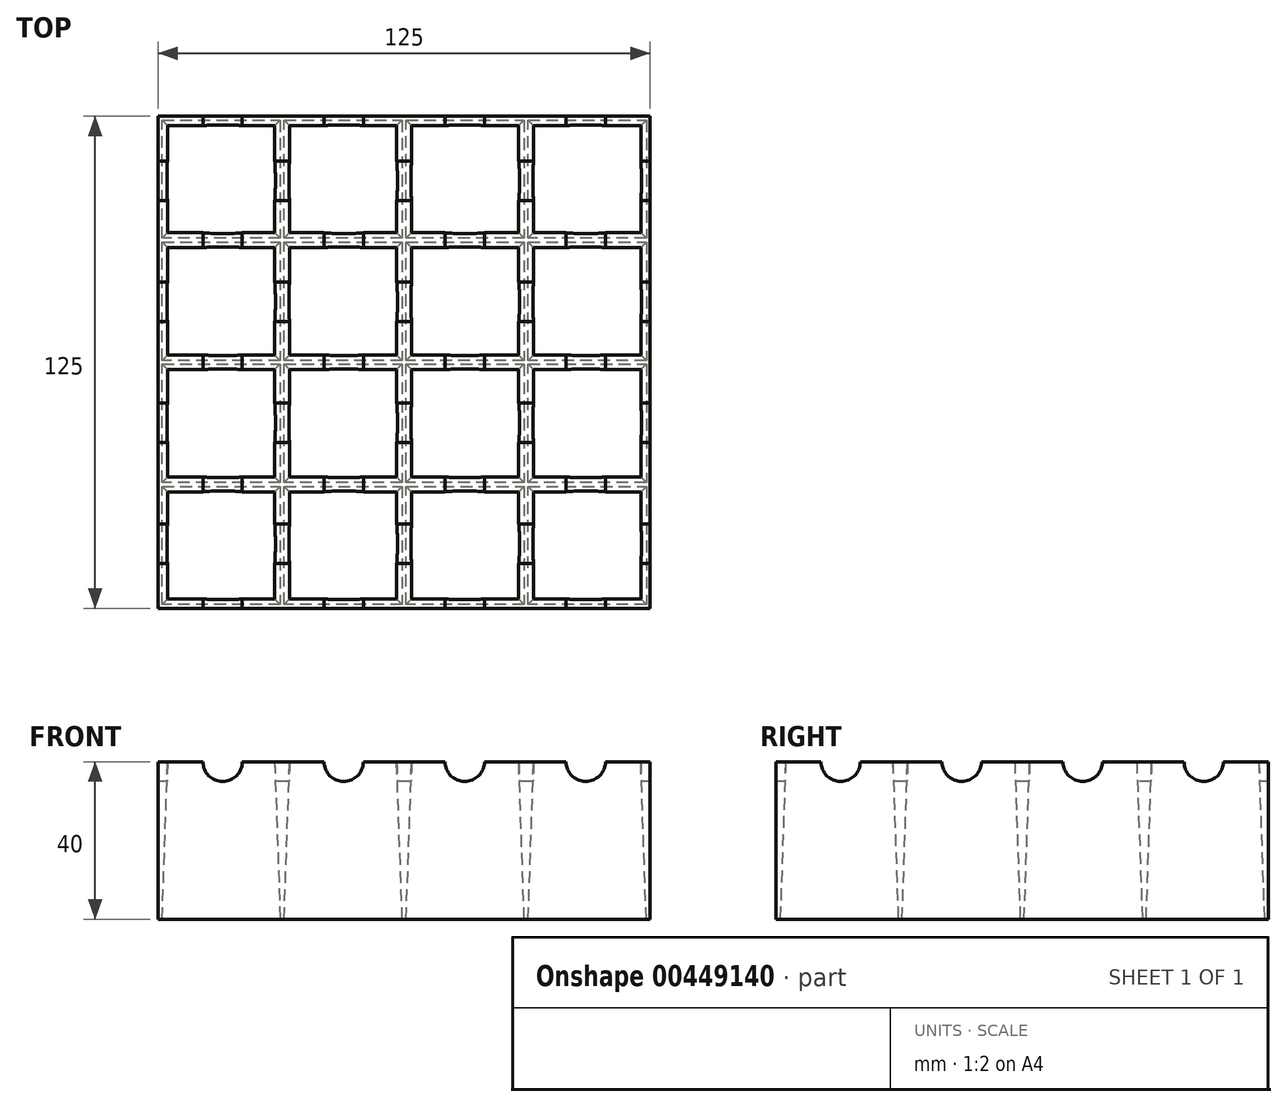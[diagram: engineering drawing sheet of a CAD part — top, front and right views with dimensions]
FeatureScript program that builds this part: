
annotation { "Feature Type Name" : "Feature", "Feature Type Description" : "" }
export const myFeature = defineFeature(function(context is Context, id is Id, definition is map)
    precondition{}
    {
        {
            var Q0;
            Q0=qCreatedBy(makeId("Top.planeOp"),FACE);
            var sketch = newSketch(context, id + "F0", { "sketchPlane" : qUnion([Q0])});
            skLineSegment(sketch, "E0.bottom", {"start": v(0, 0) * mm, "end": v(0, 0) * mm});
            skLineSegment(sketch, "E0.top", {"start": v(0, -62.5) * mm, "end": v(0, -62.5) * mm});
            skLineSegment(sketch, "E0.left", {"start": v(0, 0) * mm, "end": v(0, -62.5) * mm});
            skLineSegment(sketch, "E0.right", {"start": v(0, 0) * mm, "end": v(0, -62.5) * mm});
            skLineSegment(sketch, "E1", {"start": v(0, 0) * mm, "end": v(0, 62.5) * mm});
            skLineSegment(sketch, "E2", {"start": v(0, 0) * mm, "end": v(-62.5, 0) * mm});
            skLineSegment(sketch, "E3", {"start": v(-62.5, 0) * mm, "end": v(-62.5, 62.5) * mm});
            skLineSegment(sketch, "E4", {"start": v(0, 62.5) * mm, "end": v(-62.5, 62.5) * mm});
            skLineSegment(sketch, "E5", {"start": v(0, 62.5) * mm, "end": v(62.5, 62.5) * mm});
            skLineSegment(sketch, "E6", {"start": v(62.5, 62.5) * mm, "end": v(62.5, 0) * mm});
            skLineSegment(sketch, "E7", {"start": v(62.5, 0) * mm, "end": v(62.5, -62.5) * mm});
            skLineSegment(sketch, "E8", {"start": v(0, -62.5) * mm, "end": v(-62.5, -62.5) * mm});
            skLineSegment(sketch, "E9", {"start": v(-62.5, -62.5) * mm, "end": v(-62.5, 0) * mm});
            skLineSegment(sketch, "E10", {"start": v(0, -62.5) * mm, "end": v(62.5, -62.5) * mm});
            skSolve(sketch);
        }
        {
            var Q0;
            Q0 = qSketchRegion(id + "F0", true);
            extrude(context, id + "F1", {"entities" : qUnion([Q0]), "depth" : 40 * mm});
        }
        {
            var Q0;
            Q0=makeQuery(id+"F1.opExtrude","CAP_FACE",FACE,{"disambiguationData":[OSD([sQuery(id+"F0.wireOp",EDGE,"E3"),sQuery(id+"F0.wireOp",EDGE,"E4"),sQuery(id+"F0.wireOp",EDGE,"E5"),sQuery(id+"F0.wireOp",EDGE,"E6"),sQuery(id+"F0.wireOp",EDGE,"E7"),sQuery(id+"F0.wireOp",EDGE,"E8"),sQuery(id+"F0.wireOp",EDGE,"E9"),sQuery(id+"F0.wireOp",EDGE,"E10")])],"isStart":true});
            var sketch = newSketch(context, id + "F2", { "sketchPlane" : qUnion([Q0])});
            skLineSegment(sketch, "E11.bottom", {"start": v(-61.5, 61.5) * mm, "end": v(-31.5, 61.5) * mm});
            skLineSegment(sketch, "E11.top", {"start": v(-61.5, 31.5) * mm, "end": v(-31.5, 31.5) * mm});
            skLineSegment(sketch, "E11.left", {"start": v(-61.5, 61.5) * mm, "end": v(-61.5, 31.5) * mm});
            skLineSegment(sketch, "E11.right", {"start": v(-31.5, 61.5) * mm, "end": v(-31.5, 31.5) * mm});
            skLineSegment(sketch, "E12.0.1.0", {"start": v(-61.5, 0.5) * mm, "end": v(-31.5, 0.5) * mm});
            skLineSegment(sketch, "E12.0.1.1", {"start": v(-61.5, 30.5) * mm, "end": v(-61.5, 0.5) * mm});
            skLineSegment(sketch, "E12.0.1.2", {"start": v(-31.5, 30.5) * mm, "end": v(-31.5, 0.5) * mm});
            skLineSegment(sketch, "E12.0.1.3", {"start": v(-61.5, 30.5) * mm, "end": v(-31.5, 30.5) * mm});
            skLineSegment(sketch, "E12.0.2.0", {"start": v(-61.5, -30.5) * mm, "end": v(-31.5, -30.5) * mm});
            skLineSegment(sketch, "E12.0.2.1", {"start": v(-61.5, -0.5) * mm, "end": v(-61.5, -30.5) * mm});
            skLineSegment(sketch, "E12.0.2.2", {"start": v(-31.5, -0.5) * mm, "end": v(-31.5, -30.5) * mm});
            skLineSegment(sketch, "E12.0.2.3", {"start": v(-61.5, -0.5) * mm, "end": v(-31.5, -0.5) * mm});
            skLineSegment(sketch, "E12.0.3.0", {"start": v(-61.5, -61.5) * mm, "end": v(-31.5, -61.5) * mm});
            skLineSegment(sketch, "E12.0.3.1", {"start": v(-61.5, -31.5) * mm, "end": v(-61.5, -61.5) * mm});
            skLineSegment(sketch, "E12.0.3.2", {"start": v(-31.5, -31.5) * mm, "end": v(-31.5, -61.5) * mm});
            skLineSegment(sketch, "E12.0.3.3", {"start": v(-61.5, -31.5) * mm, "end": v(-31.5, -31.5) * mm});
            skLineSegment(sketch, "E12.1.0.0", {"start": v(-30.5, 31.5) * mm, "end": v(-0.5, 31.5) * mm});
            skLineSegment(sketch, "E12.1.0.1", {"start": v(-30.5, 61.5) * mm, "end": v(-30.5, 31.5) * mm});
            skLineSegment(sketch, "E12.1.0.2", {"start": v(-0.5, 61.5) * mm, "end": v(-0.5, 31.5) * mm});
            skLineSegment(sketch, "E12.1.0.3", {"start": v(-30.5, 61.5) * mm, "end": v(-0.5, 61.5) * mm});
            skLineSegment(sketch, "E12.1.1.0", {"start": v(-30.5, 0.5) * mm, "end": v(-0.5, 0.5) * mm});
            skLineSegment(sketch, "E12.1.1.1", {"start": v(-30.5, 30.5) * mm, "end": v(-30.5, 0.5) * mm});
            skLineSegment(sketch, "E12.1.1.2", {"start": v(-0.5, 30.5) * mm, "end": v(-0.5, 0.5) * mm});
            skLineSegment(sketch, "E12.1.1.3", {"start": v(-30.5, 30.5) * mm, "end": v(-0.5, 30.5) * mm});
            skLineSegment(sketch, "E12.1.2.0", {"start": v(-30.5, -30.5) * mm, "end": v(-0.5, -30.5) * mm});
            skLineSegment(sketch, "E12.1.2.1", {"start": v(-30.5, -0.5) * mm, "end": v(-30.5, -30.5) * mm});
            skLineSegment(sketch, "E12.1.2.2", {"start": v(-0.5, -0.5) * mm, "end": v(-0.5, -30.5) * mm});
            skLineSegment(sketch, "E12.1.2.3", {"start": v(-30.5, -0.5) * mm, "end": v(-0.5, -0.5) * mm});
            skLineSegment(sketch, "E12.1.3.0", {"start": v(-30.5, -61.5) * mm, "end": v(-0.5, -61.5) * mm});
            skLineSegment(sketch, "E12.1.3.1", {"start": v(-30.5, -31.5) * mm, "end": v(-30.5, -61.5) * mm});
            skLineSegment(sketch, "E12.1.3.2", {"start": v(-0.5, -31.5) * mm, "end": v(-0.5, -61.5) * mm});
            skLineSegment(sketch, "E12.1.3.3", {"start": v(-30.5, -31.5) * mm, "end": v(-0.5, -31.5) * mm});
            skLineSegment(sketch, "E12.2.0.0", {"start": v(0.5, 31.5) * mm, "end": v(30.5, 31.5) * mm});
            skLineSegment(sketch, "E12.2.0.1", {"start": v(0.5, 61.5) * mm, "end": v(0.5, 31.5) * mm});
            skLineSegment(sketch, "E12.2.0.2", {"start": v(30.5, 61.5) * mm, "end": v(30.5, 31.5) * mm});
            skLineSegment(sketch, "E12.2.0.3", {"start": v(0.5, 61.5) * mm, "end": v(30.5, 61.5) * mm});
            skLineSegment(sketch, "E12.2.1.0", {"start": v(0.5, 0.5) * mm, "end": v(30.5, 0.5) * mm});
            skLineSegment(sketch, "E12.2.1.1", {"start": v(0.5, 30.5) * mm, "end": v(0.5, 0.5) * mm});
            skLineSegment(sketch, "E12.2.1.2", {"start": v(30.5, 30.5) * mm, "end": v(30.5, 0.5) * mm});
            skLineSegment(sketch, "E12.2.1.3", {"start": v(0.5, 30.5) * mm, "end": v(30.5, 30.5) * mm});
            skLineSegment(sketch, "E12.2.2.0", {"start": v(0.5, -30.5) * mm, "end": v(30.5, -30.5) * mm});
            skLineSegment(sketch, "E12.2.2.1", {"start": v(0.5, -0.5) * mm, "end": v(0.5, -30.5) * mm});
            skLineSegment(sketch, "E12.2.2.2", {"start": v(30.5, -0.5) * mm, "end": v(30.5, -30.5) * mm});
            skLineSegment(sketch, "E12.2.2.3", {"start": v(0.5, -0.5) * mm, "end": v(30.5, -0.5) * mm});
            skLineSegment(sketch, "E12.2.3.0", {"start": v(0.5, -61.5) * mm, "end": v(30.5, -61.5) * mm});
            skLineSegment(sketch, "E12.2.3.1", {"start": v(0.5, -31.5) * mm, "end": v(0.5, -61.5) * mm});
            skLineSegment(sketch, "E12.2.3.2", {"start": v(30.5, -31.5) * mm, "end": v(30.5, -61.5) * mm});
            skLineSegment(sketch, "E12.2.3.3", {"start": v(0.5, -31.5) * mm, "end": v(30.5, -31.5) * mm});
            skLineSegment(sketch, "E12.3.0.0", {"start": v(31.5, 31.5) * mm, "end": v(61.5, 31.5) * mm});
            skLineSegment(sketch, "E12.3.0.1", {"start": v(31.5, 61.5) * mm, "end": v(31.5, 31.5) * mm});
            skLineSegment(sketch, "E12.3.0.2", {"start": v(61.5, 61.5) * mm, "end": v(61.5, 31.5) * mm});
            skLineSegment(sketch, "E12.3.0.3", {"start": v(31.5, 61.5) * mm, "end": v(61.5, 61.5) * mm});
            skLineSegment(sketch, "E12.3.1.0", {"start": v(31.5, 0.5) * mm, "end": v(61.5, 0.5) * mm});
            skLineSegment(sketch, "E12.3.1.1", {"start": v(31.5, 30.5) * mm, "end": v(31.5, 0.5) * mm});
            skLineSegment(sketch, "E12.3.1.2", {"start": v(61.5, 30.5) * mm, "end": v(61.5, 0.5) * mm});
            skLineSegment(sketch, "E12.3.1.3", {"start": v(31.5, 30.5) * mm, "end": v(61.5, 30.5) * mm});
            skLineSegment(sketch, "E12.3.2.0", {"start": v(31.5, -30.5) * mm, "end": v(61.5, -30.5) * mm});
            skLineSegment(sketch, "E12.3.2.1", {"start": v(31.5, -0.5) * mm, "end": v(31.5, -30.5) * mm});
            skLineSegment(sketch, "E12.3.2.2", {"start": v(61.5, -0.5) * mm, "end": v(61.5, -30.5) * mm});
            skLineSegment(sketch, "E12.3.2.3", {"start": v(31.5, -0.5) * mm, "end": v(61.5, -0.5) * mm});
            skLineSegment(sketch, "E12.3.3.0", {"start": v(31.5, -61.5) * mm, "end": v(61.5, -61.5) * mm});
            skLineSegment(sketch, "E12.3.3.1", {"start": v(31.5, -31.5) * mm, "end": v(31.5, -61.5) * mm});
            skLineSegment(sketch, "E12.3.3.2", {"start": v(61.5, -31.5) * mm, "end": v(61.5, -61.5) * mm});
            skLineSegment(sketch, "E12.3.3.3", {"start": v(31.5, -31.5) * mm, "end": v(61.5, -31.5) * mm});
            skLineSegment(sketch, "E12.direction1", {"start": v(-61.5, 31.5) * mm, "end": v(-30.5, 31.5) * mm, "construction": true});
            skLineSegment(sketch, "E12.direction2", {"start": v(-61.5, 31.5) * mm, "end": v(-61.5, 0.5) * mm, "construction": true});
            skSolve(sketch);
        }
        {
            var Q0;
            Q0 = qSketchRegion(id + "F2", true);
            extrude(context, id + "F3", {"entities" : qUnion([Q0]), "operationType" : NewBodyOperationType.REMOVE, "endBound" : BoundingType.UP_TO_NEXT, "oppositeDirection" : true, "depth" : 25 * mm, "hasDraft" : true, "draftAngle" : 2 * degree, "draftPullDirection" : true});
        }
        {
            var Q0;
            Q0=makeQuery(id+"F1.opExtrude","SWEPT_FACE",FACE,{"disambiguationData":[OSD([sQuery(id+"F0.wireOp",EDGE,"E8"),sQuery(id+"F0.wireOp",EDGE,"E10")])]});
            var sketch = newSketch(context, id + "F4", { "sketchPlane" : qUnion([Q0])});
            skArc(sketch, "E13", {"start": v(10.37, 40) * mm, "mid": v(15.37, 35) * mm, "end": v(20.37, 40) * mm});
            skArc(sketch, "E14", {"start": v(41.12, 40) * mm, "mid": v(46.12, 35) * mm, "end": v(51.12, 40) * mm});
            skArc(sketch, "E15", {"start": v(-20.38, 40) * mm, "mid": v(-15.38, 35) * mm, "end": v(-10.37, 40) * mm});
            skArc(sketch, "E16", {"start": v(-51.12, 40) * mm, "mid": v(-46.12, 35) * mm, "end": v(-41.12, 40) * mm});
            skLineSegment(sketch, "E17", {"start": v(-51.13, 40) * mm, "end": v(-41.13, 40) * mm});
            skLineSegment(sketch, "E18.trimOffspring", {"start": v(-20.38, 40) * mm, "end": v(-10.37, 40) * mm});
            skLineSegment(sketch, "E19.trimOffspring", {"start": v(10.37, 40) * mm, "end": v(20.37, 40) * mm});
            skLineSegment(sketch, "E20.trimOffspring", {"start": v(41.12, 40) * mm, "end": v(51.12, 40) * mm});
            skSolve(sketch);
        }
        {
            var Q0;
            Q0 = qSketchRegion(id + "F4", true);
            var Q1;
            Q1=makeQuery(id+"F1.opExtrude","SWEPT_FACE",FACE,{"disambiguationData":[OSD([sQuery(id+"F0.wireOp",EDGE,"E4"),sQuery(id+"F0.wireOp",EDGE,"E5")])]});
            extrude(context, id + "F5", {"entities" : qUnion([Q0]), "operationType" : NewBodyOperationType.REMOVE, "endBound" : BoundingType.UP_TO_SURFACE, "oppositeDirection" : true, "endBoundEntityFace" : qUnion([Q1]), "depth" : 25 * mm});
        }
        {
            var Q0;
            Q0=makeQuery(id+"F1.opExtrude","SWEPT_FACE",FACE,{"disambiguationData":[OSD([sQuery(id+"F0.wireOp",EDGE,"E3"),sQuery(id+"F0.wireOp",EDGE,"E9")])]});
            var sketch = newSketch(context, id + "F6", { "sketchPlane" : qUnion([Q0])});
            skArc(sketch, "E21", {"start": v(-51.12, 40) * mm, "mid": v(-46.12, 35) * mm, "end": v(-41.12, 40) * mm});
            skArc(sketch, "E22", {"start": v(-20.38, 40) * mm, "mid": v(-15.38, 35) * mm, "end": v(-10.37, 40) * mm});
            skArc(sketch, "E23", {"start": v(10.37, 40) * mm, "mid": v(15.38, 35) * mm, "end": v(20.38, 40) * mm});
            skArc(sketch, "E24", {"start": v(41.12, 40) * mm, "mid": v(46.12, 35) * mm, "end": v(51.12, 40) * mm});
            skLineSegment(sketch, "E25", {"start": v(-62.5, 40) * mm, "end": v(51.13, 40) * mm});
            skLineSegment(sketch, "E26", {"start": v(-51.12, 40) * mm, "end": v(-46.12, 40) * mm});
            skLineSegment(sketch, "E27", {"start": v(-46.12, 40) * mm, "end": v(-41.12, 40) * mm});
            skLineSegment(sketch, "E28", {"start": v(-15.38, 40) * mm, "end": v(-10.37, 40) * mm});
            skLineSegment(sketch, "E29", {"start": v(15.38, 40) * mm, "end": v(20.38, 40) * mm});
            skLineSegment(sketch, "E30.trimOffspring", {"start": v(-20.38, 40) * mm, "end": v(-15.38, 40) * mm});
            skLineSegment(sketch, "E31.trimOffspring", {"start": v(10.37, 40) * mm, "end": v(15.38, 40) * mm});
            skLineSegment(sketch, "E32.trimOffspring", {"start": v(41.12, 40) * mm, "end": v(46.12, 40) * mm});
            skSolve(sketch);
        }
        {
            var Q0;
            Q0 = qSketchRegion(id + "F6", true);
            var Q1;
            Q1=makeQuery(id+"F1.opExtrude","SWEPT_FACE",FACE,{"disambiguationData":[OSD([sQuery(id+"F0.wireOp",EDGE,"E6"),sQuery(id+"F0.wireOp",EDGE,"E7")])]});
            extrude(context, id + "F7", {"entities" : qUnion([Q0]), "operationType" : NewBodyOperationType.REMOVE, "endBound" : BoundingType.UP_TO_SURFACE, "oppositeDirection" : true, "endBoundEntityFace" : qUnion([Q1]), "depth" : 25 * mm});
        }
    });
